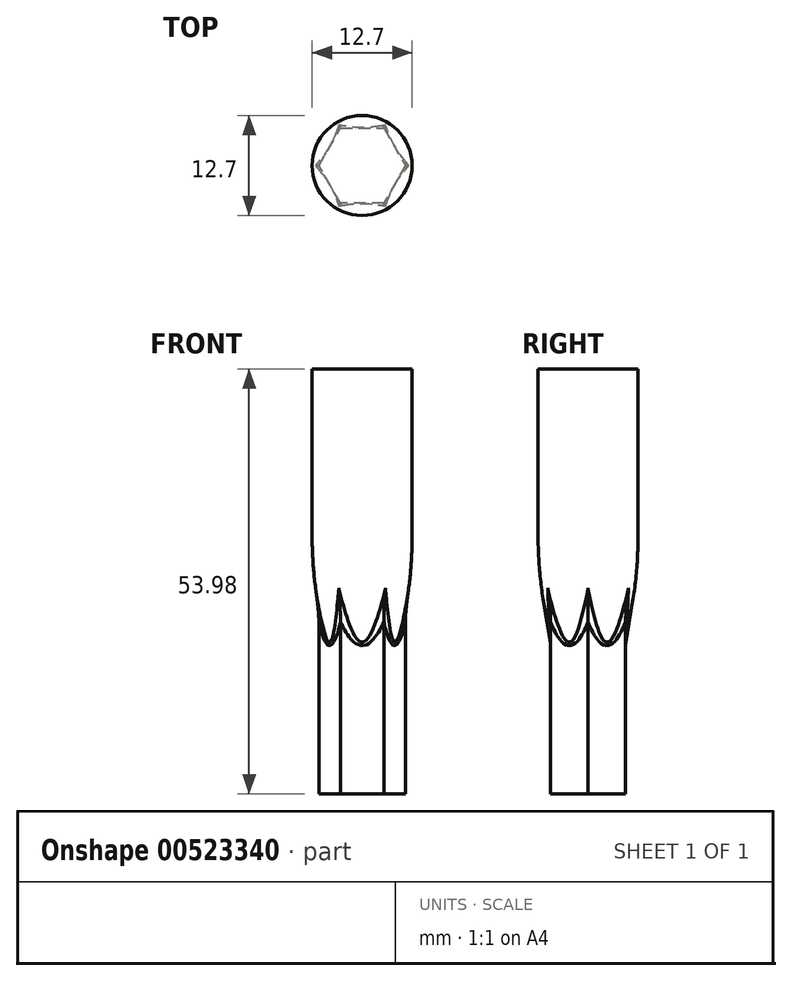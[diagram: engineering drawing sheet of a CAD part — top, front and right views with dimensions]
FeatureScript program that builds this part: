
annotation { "Feature Type Name" : "Feature", "Feature Type Description" : "" }
export const myFeature = defineFeature(function(context is Context, id is Id, definition is map)
    precondition{}
    {
        {
            var Q0;
            Q0=qCreatedBy(makeId("Top.planeOp"),FACE);
            var sketch = newSketch(context, id + "F0", { "sketchPlane" : qUnion([Q0])});
            skCircle(sketch, "E0.cCircle", {"center": v(0, 0) * mm, "radius": 4.76 * mm, "construction": true});
            skLineSegment(sketch, "E0.0", {"start": v(2.75, 4.76) * mm, "end": v(5.5, 0) * mm});
            skLineSegment(sketch, "E0.1", {"start": v(5.5, 0) * mm, "end": v(2.75, -4.76) * mm});
            skLineSegment(sketch, "E0.2", {"start": v(2.75, -4.76) * mm, "end": v(-2.75, -4.76) * mm});
            skLineSegment(sketch, "E0.3", {"start": v(-2.75, -4.76) * mm, "end": v(-5.5, 0) * mm});
            skLineSegment(sketch, "E0.4", {"start": v(-5.5, 0) * mm, "end": v(-2.75, 4.76) * mm});
            skLineSegment(sketch, "E0.5", {"start": v(-2.75, 4.76) * mm, "end": v(2.75, 4.76) * mm});
            skPoint(sketch, "E0.0.midPoint", {"position": v(4.12, 2.38) * mm});
            skSolve(sketch);
        }
        {
            var Q0;
            Q0=makeQuery(id+"F0.imprint","IMPRINT",FACE,{"disambiguationData":[TD([[makeQuery(id+"F0.imprint","IMPRINT",EDGE,{"derivedFrom":sQuery(id+"F0.wireOp",EDGE,"E0.0")}),-1.0]])]});
            extrude(context, id + "F1", {"entities" : qUnion([Q0]), "depth" : 25.4 * mm, "offsetDistance" : 25.4 * mm});
        }
        {
            var Q0;
            Q0=qCreatedBy(makeId("Right.planeOp"),FACE);
            var sketch = newSketch(context, id + "F2", { "sketchPlane" : qUnion([Q0])});
            skLineSegment(sketch, "E1", {"start": v(0, 0) * mm, "end": v(0, 60.61) * mm, "construction": true});
            skLineSegment(sketch, "E2", {"start": v(0, 53.98) * mm, "end": v(-6.35, 53.98) * mm});
            skLineSegment(sketch, "E3", {"start": v(-6.35, 53.98) * mm, "end": v(-6.35, 32.78) * mm});
            skLineSegment(sketch, "E4", {"start": v(-5.66, 24.43) * mm, "end": v(-4.76, 19.05) * mm});
            skLineSegment(sketch, "E5", {"start": v(-4.76, 19.05) * mm, "end": v(0, 19.05) * mm});
            skLineSegment(sketch, "E6", {"start": v(0, 19.05) * mm, "end": v(0, 53.98) * mm});
            skPoint(sketch, "E7.visualSharp", {"position": v(-6.35, 28.58) * mm});
            skArc(sketch, "E7.filletArc", {"start": v(-6.35, 32.78) * mm, "mid": v(-6.18, 28.59) * mm, "end": v(-5.66, 24.43) * mm});
            skSolve(sketch);
        }
        {
            var Q0;
            Q0=makeQuery(id+"F2.imprint","IMPRINT",FACE,{"disambiguationData":[TD([[makeQuery(id+"F2.imprint","IMPRINT",EDGE,{"derivedFrom":sQuery(id+"F2.wireOp",EDGE,"E2")}),1.0]])]});
            var Q1;
            Q1=sQuery(id+"F2.wireOp",EDGE,"E1");
            revolve(context, id + "F3", {"operationType" : NewBodyOperationType.ADD, "entities" : qUnion([Q0]), "axis" : qUnion([Q1]), "revolveType" : RevolveType.FULL});
        }
        {
            var Q0;
            Q0=makeQuery(id+"F3.boolean.opBoolean","SPLIT",FACE,{"disambiguationData":[TD([makeQuery(id+"F1.opExtrude","SWEPT_FACE",FACE,{"disambiguationData":[OSD([sQuery(id+"F0.wireOp",EDGE,"E0.4")])]})])],"derivedFrom":makeQuery(id+"F3.opRevolve","SWEPT_FACE",FACE,{"disambiguationData":[OSD([sQuery(id+"F2.wireOp",EDGE,"E4")])]})});
            var Q1;
            Q1=makeQuery(id+"F3.boolean.opBoolean","SPLIT",FACE,{"disambiguationData":[TD([makeQuery(id+"F1.opExtrude","SWEPT_FACE",FACE,{"disambiguationData":[OSD([sQuery(id+"F0.wireOp",EDGE,"E0.3")])]})])],"derivedFrom":makeQuery(id+"F3.opRevolve","SWEPT_FACE",FACE,{"disambiguationData":[OSD([sQuery(id+"F2.wireOp",EDGE,"E4")])]})});
            var Q2;
            Q2=makeQuery(id+"F3.boolean.opBoolean","SPLIT",FACE,{"disambiguationData":[TD([makeQuery(id+"F1.opExtrude","SWEPT_FACE",FACE,{"disambiguationData":[OSD([sQuery(id+"F0.wireOp",EDGE,"E0.0")])]})])],"derivedFrom":makeQuery(id+"F3.opRevolve","SWEPT_FACE",FACE,{"disambiguationData":[OSD([sQuery(id+"F2.wireOp",EDGE,"E4")])]})});
            var Q3;
            Q3=makeQuery(id+"F3.boolean.opBoolean","SPLIT",FACE,{"disambiguationData":[TD([makeQuery(id+"F1.opExtrude","SWEPT_FACE",FACE,{"disambiguationData":[OSD([sQuery(id+"F0.wireOp",EDGE,"E0.1")])]})])],"derivedFrom":makeQuery(id+"F3.opRevolve","SWEPT_FACE",FACE,{"disambiguationData":[OSD([sQuery(id+"F2.wireOp",EDGE,"E4")])]})});
            var Q4;
            Q4=makeQuery(id+"F3.boolean.opBoolean","SPLIT",FACE,{"disambiguationData":[TD([makeQuery(id+"F1.opExtrude","SWEPT_FACE",FACE,{"disambiguationData":[OSD([sQuery(id+"F0.wireOp",EDGE,"E0.2")])]})])],"derivedFrom":makeQuery(id+"F3.opRevolve","SWEPT_FACE",FACE,{"disambiguationData":[OSD([sQuery(id+"F2.wireOp",EDGE,"E4")])]})});
            var Q5;
            Q5=makeQuery(id+"F3.boolean.opBoolean","SPLIT",FACE,{"disambiguationData":[TD([makeQuery(id+"F1.opExtrude","SWEPT_FACE",FACE,{"disambiguationData":[OSD([sQuery(id+"F0.wireOp",EDGE,"E0.5")])]})])],"derivedFrom":makeQuery(id+"F3.opRevolve","SWEPT_FACE",FACE,{"disambiguationData":[OSD([sQuery(id+"F2.wireOp",EDGE,"E4")])]})});
            fillet(context, id + "F4", {"entities" : qUnion([Q0, Q1, Q2, Q3, Q4, Q5]), "radius" : 2.54 * mm, "tangentPropagation" : true, "allowEdgeOverflow" : false});
        }
    });
